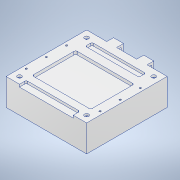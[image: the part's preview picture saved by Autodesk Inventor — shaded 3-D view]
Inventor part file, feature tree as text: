
AUTODESK INVENTOR PART (.ipt)
format: ipt  version: 2022 (Build 260153000, 153)  size: 237,056 bytes
history: native  units: in
note: dims shown in document units (in); Inventor stores cm internally (conversion verified against a paired STEP export)
features: sketch x8, extrude x5, hole x3
ambient origin geometry x8: Origin, YZ Plane, XZ Plane, XY Plane, X Axis, Y Axis, Z Axis, Center Point
bodies: Solid1 (feature_tree)
feature tree (16):
  extrude  "Extrusion1"  Depth=3.25in
  extrude  "Extrusion2"  Depth=0.375in
  extrude  "Extrusion3"  Depth=0.25in
  hole  "Hole1"  [1 undecoded]
  extrude  "Extrusion5"  Depth=0.125in
  hole  "Hole2"  [1 undecoded]
  hole  "Hole3"  [1 undecoded]
  extrude  "Extrusion6"  Depth=2.0in
  sketch  "Sketch1"  dims[d0=3.0in d1=3.25in]
  sketch  "Sketch2"  dims[d2=1.0in d3=0.0in d6=0.375in]
  sketch  "Sketch3"  dims[d7=0.375in d8=0.25in]
  sketch  "Sketch4"  dims[d9=0.75in d10=0.0in d11=0.0in]
  sketch  "Sketch6"  dims[d12=0.0in d13=0.0in d14=0.125in]
  sketch  "Sketch7"  dims[d15=0.125in]
  sketch  "Sketch8"  dims[d16=0.1in d17=0.38in d18=0.375in d19=0.25in d20=0.5635in d21=1.0in d22=0.8108in d25=2.0in]
  sketch  "Sketch9"  dims[d26=0.25in d28=0.5in d29=2.0in d30=0.25in d31=0.5in d32=0.0938in d33=0.0in d34=0.75in d35=0.75in d36=0.125in d37=0.0667in d38=0.172in d39=0.156in d40=0.073in d41=0.5635in d42=1.0in d43=0.8108in d44=1.375in d46=0.0625in d47=0.25in d48=0.25in d50=0.25in d51=0.081in d52=0.38in d53=0.156in d54=0.073in d55=0.5635in d56=1.0in d57=0.8108in d58=0.26in d60=0.3in d61=0.25in d62=0.3644in d63=0.5144in d64=2.1813in d65=1.6213in d66=0.1181in d67=0.0in d68=0.0625in]
note: 3 required parameter values undecoded (feature->parameter linkage not recoverable at this tier; creation-order binding heuristic only, values carry confidence <= 0.55)
